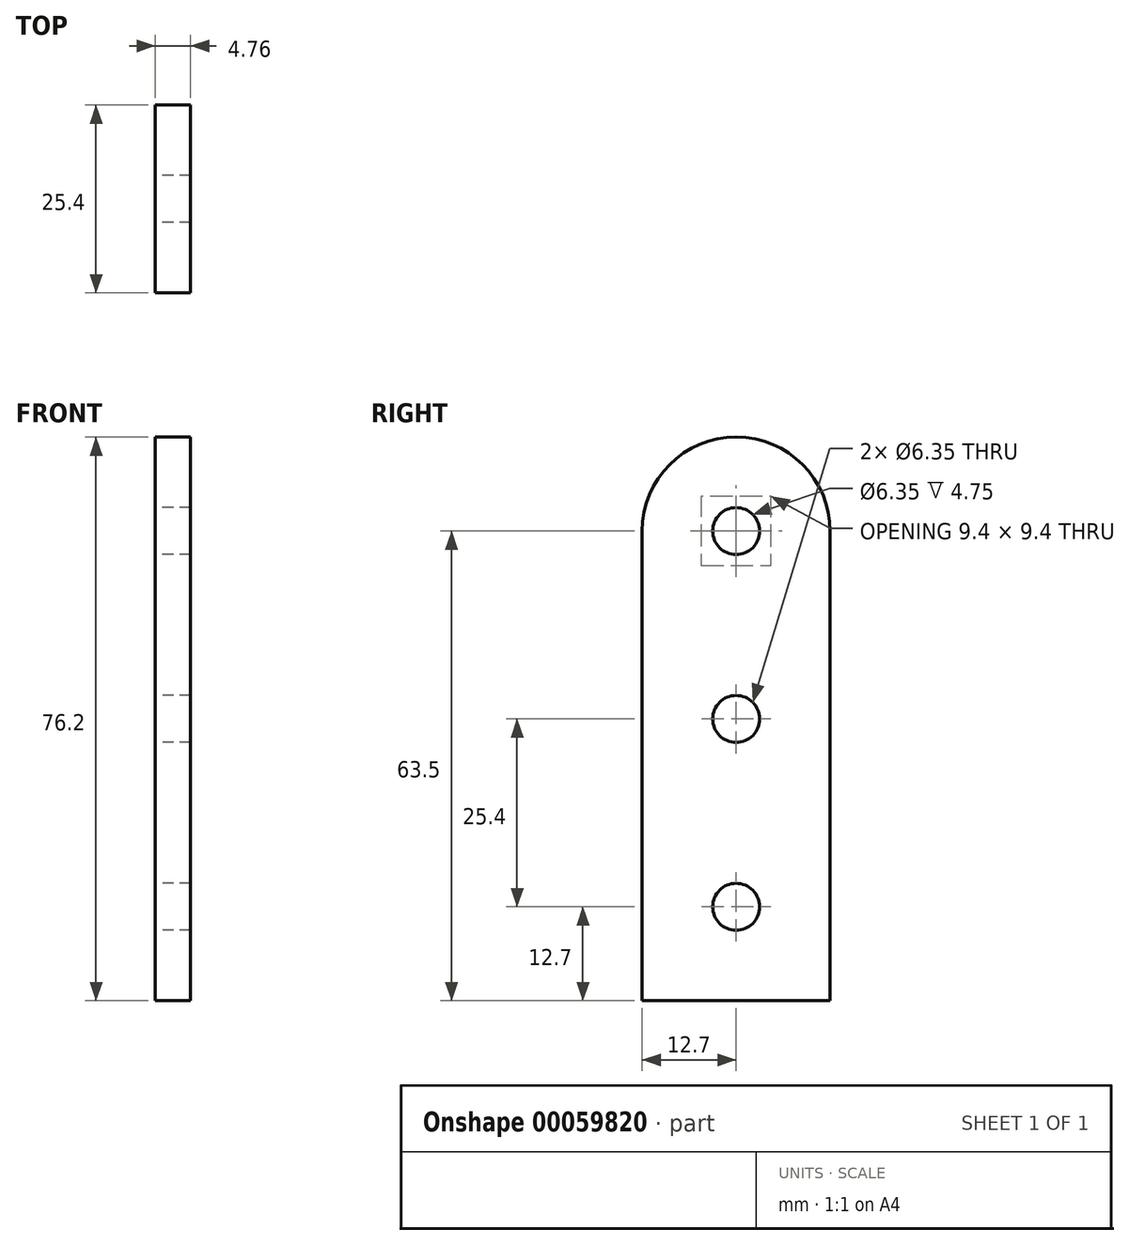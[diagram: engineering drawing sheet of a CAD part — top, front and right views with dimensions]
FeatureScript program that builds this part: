
annotation { "Feature Type Name" : "Feature", "Feature Type Description" : "" }
export const myFeature = defineFeature(function(context is Context, id is Id, definition is map)
    precondition{}
    {
        {
            var Q0;
            Q0=qCreatedBy(makeId("Right.planeOp"),FACE);
            var sketch = newSketch(context, id + "F0", { "sketchPlane" : qUnion([Q0])});
            skLineSegment(sketch, "E0.bottom", {"start": v(0, 0) * mm, "end": v(-25.4, 0) * mm});
            skLineSegment(sketch, "E0.top", {"start": v(0, 63.5) * mm, "end": v(-25.4, 63.5) * mm});
            skLineSegment(sketch, "E0.left", {"start": v(0, 0) * mm, "end": v(0, 63.5) * mm});
            skLineSegment(sketch, "E0.right", {"start": v(-25.4, 0) * mm, "end": v(-25.4, 63.5) * mm});
            skArc(sketch, "E1", {"start": v(0, 63.5) * mm, "mid": v(-12.7, 76.2) * mm, "end": v(-25.4, 63.5) * mm});
            skCircle(sketch, "E2", {"center": v(-12.7, 12.7) * mm, "radius": 3.18 * mm});
            skPoint(sketch, "E3", {"position": v(-12.7, 0) * mm});
            skCircle(sketch, "E4", {"center": v(-12.7, 38.1) * mm, "radius": 3.18 * mm});
            skCircle(sketch, "E5", {"center": v(-12.7, 63.5) * mm, "radius": 3.18 * mm});
            skCircle(sketch, "E6", {"center": v(-12.7, 63.5) * mm, "radius": 4.7 * mm});
            skSolve(sketch);
        }
        {
            var Q0;
            Q0=makeQuery(id+"F0.imprint","IMPRINT",FACE,{"disambiguationData":[TD([[makeQuery(id+"F0.imprint","IMPRINT",EDGE,{"derivedFrom":sQuery(id+"F0.wireOp",EDGE,"E0.bottom")}),-1.0]])]});
            var Q1;
            {var subQ0=sQuery(id+"F0.wireOp",EDGE,"E1");Q1=makeQuery(id+"F0.imprint","IMPRINT",FACE,{"disambiguationData":[TD([[makeQuery(id+"F0.imprint","IMPRINT",EDGE,{"derivedFrom":subQ0}),1.0]])]});}
            extrude(context, id + "F1", {"entities" : qUnion([Q0, Q1]), "depth" : 4.76 * mm, "symmetric" : true});
        }
        {
            var Q0;
            Q0=qCreatedBy(makeId("Right.planeOp"),FACE);
            var sketch = newSketch(context, id + "F2", { "sketchPlane" : qUnion([Q0])});
            skCircle(sketch, "E7.0", {"center": v(-12.7, 63.5) * mm, "radius": 4.7 * mm});
            skCircle(sketch, "E8.0", {"center": v(-12.7, 63.5) * mm, "radius": 3.18 * mm});
            skSolve(sketch);
        }
        {
            var Q0;
            Q0 = qSketchRegion(id + "F2", true);
            var Q1;
            Q1=makeQuery(id+"F1.opExtrude","CAP_FACE",FACE,{"disambiguationData":[OSD([sQuery(id+"F0.wireOp",EDGE,"E0.bottom"),sQuery(id+"F0.wireOp",EDGE,"E0.left"),sQuery(id+"F0.wireOp",EDGE,"E0.right"),sQuery(id+"F0.wireOp",EDGE,"E1"),sQuery(id+"F0.wireOp",EDGE,"E2"),sQuery(id+"F0.wireOp",EDGE,"E4"),sQuery(id+"F0.wireOp",EDGE,"E6")])],"isStart":false});
            var Q2;
            Q2=makeQuery(id+"F1.opExtrude","CAP_FACE",FACE,{"disambiguationData":[OSD([sQuery(id+"F0.wireOp",EDGE,"E0.bottom"),sQuery(id+"F0.wireOp",EDGE,"E0.left"),sQuery(id+"F0.wireOp",EDGE,"E0.right"),sQuery(id+"F0.wireOp",EDGE,"E1"),sQuery(id+"F0.wireOp",EDGE,"E2"),sQuery(id+"F0.wireOp",EDGE,"E4"),sQuery(id+"F0.wireOp",EDGE,"E6")])],"isStart":true});
            extrude(context, id + "F3", {"entities" : qUnion([Q0]), "operationType" : NewBodyOperationType.ADD, "endBoundEntityFace" : qUnion([Q1]), "depth" : 4.75 * mm, "hasSecondDirection" : true, "secondDirectionBound" : BoundingType.UP_TO_SURFACE, "secondDirectionOppositeDirection" : true, "secondDirectionBoundEntityFace" : qUnion([Q2]), "secondDirectionDepth" : 25.4 * mm, "symmetric" : true});
        }
    });
